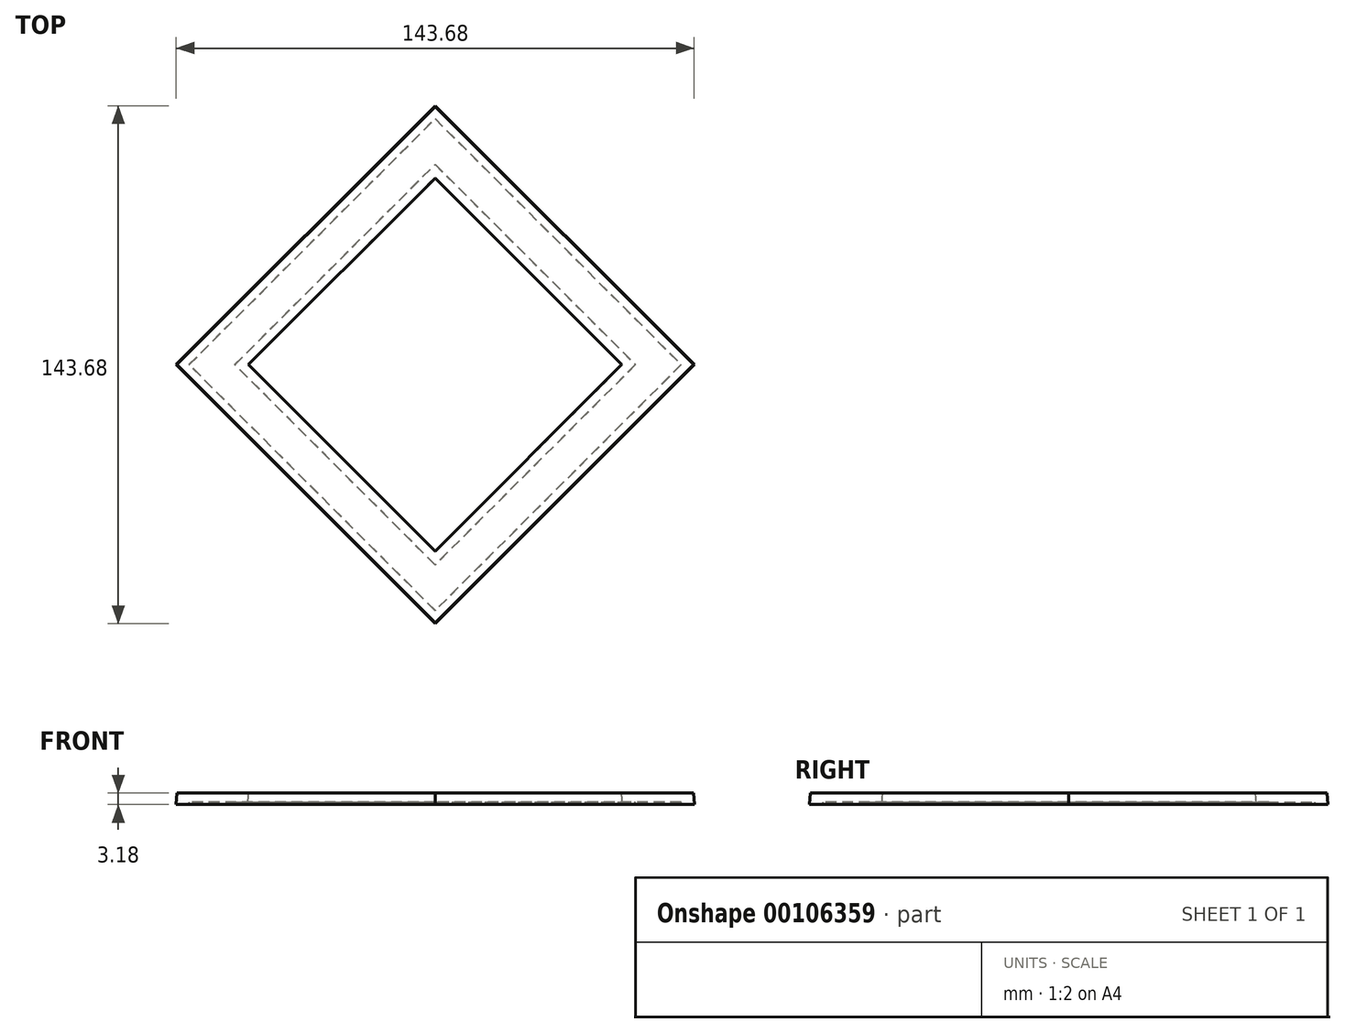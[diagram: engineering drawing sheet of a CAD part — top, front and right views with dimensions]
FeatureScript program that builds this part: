
annotation { "Feature Type Name" : "Feature", "Feature Type Description" : "" }
export const myFeature = defineFeature(function(context is Context, id is Id, definition is map)
    precondition{}
    {
        {
            var Q0;
            Q0=qCreatedBy(makeId("Top.planeOp"),FACE);
            var sketch = newSketch(context, id + "F0", { "sketchPlane" : qUnion([Q0])});
            skLineSegment(sketch, "E0.bottom", {"start": v(50.8, -50.8) * mm, "end": v(-50.8, -50.8) * mm});
            skLineSegment(sketch, "E0.top", {"start": v(50.8, 50.8) * mm, "end": v(-50.8, 50.8) * mm});
            skLineSegment(sketch, "E0.left", {"start": v(50.8, -50.8) * mm, "end": v(50.8, 50.8) * mm});
            skLineSegment(sketch, "E0.right", {"start": v(-50.8, -50.8) * mm, "end": v(-50.8, 50.8) * mm});
            skPoint(sketch, "E0.middle", {"position": v(0, 0) * mm});
            skSolve(sketch);
        }
        {
            var Q0;
            Q0 = qSketchRegion(id + "F0", true);
            extrude(context, id + "F1", {"entities" : qUnion([Q0]), "depth" : 3.17 * mm, "hasDraft" : true, "draftAngle" : 3 * degree, "draftPullDirection" : true});
        }
        {
            var Q0;
            Q0=makeQuery(id+"F1.opExtrude","CAP_FACE",FACE,{"disambiguationData":[OSD([sQuery(id+"F0.wireOp",EDGE,"E0.bottom"),sQuery(id+"F0.wireOp",EDGE,"E0.top"),sQuery(id+"F0.wireOp",EDGE,"E0.left"),sQuery(id+"F0.wireOp",EDGE,"E0.right")])],"isStart":false});
            var Q1;
            Q1=makeQuery(id+"F1.opExtrude","CAP_FACE",FACE,{"disambiguationData":[OSD([sQuery(id+"F0.wireOp",EDGE,"E0.bottom"),sQuery(id+"F0.wireOp",EDGE,"E0.top"),sQuery(id+"F0.wireOp",EDGE,"E0.left"),sQuery(id+"F0.wireOp",EDGE,"E0.right")])],"isStart":true});
            shell(context, id + "F2", {"entities" : qUnion([Q0, Q1]), "thickness" : 14.03 * mm});
        }
        {
            var Q0;
            Q0=qCreatedBy(makeId("Front.planeOp"),FACE);
            var sketch = newSketch(context, id + "F3", { "sketchPlane" : qUnion([Q0])});
            skLineSegment(sketch, "E1", {"start": v(0, 0) * mm, "end": v(0, 138.81) * mm});
            skSolve(sketch);
        }
        {
            var Q0;
            Q0=makeQuery(id+"F1.opExtrude","SWEPT_BODY",BODY,{"disambiguationData":[OSD([sQuery(id+"F0.wireOp",EDGE,"E0.bottom"),sQuery(id+"F0.wireOp",EDGE,"E0.top"),sQuery(id+"F0.wireOp",EDGE,"E0.left"),sQuery(id+"F0.wireOp",EDGE,"E0.right")])]});
            var Q1;
            Q1=sQuery(id+"F3.wireOp",EDGE,"E1");
            transform(context, id + "F4", {"entities" : qUnion([Q0]), "transformType" : TransformType.ROTATION, "transformAxis" : qUnion([Q1]), "angle" : 45 * degree, "makeCopy" : false});
        }
        {
            var Q0;
            Q0=makeQuery(id+"F1.opExtrude","CAP_FACE",FACE,{"disambiguationData":[OSD([sQuery(id+"F0.wireOp",EDGE,"E0.bottom"),sQuery(id+"F0.wireOp",EDGE,"E0.top"),sQuery(id+"F0.wireOp",EDGE,"E0.left"),sQuery(id+"F0.wireOp",EDGE,"E0.right")])],"isStart":true});
            shell(context, id + "F5", {"entities" : qUnion([Q0]), "thickness" : 2.54 * mm});
        }
    });
